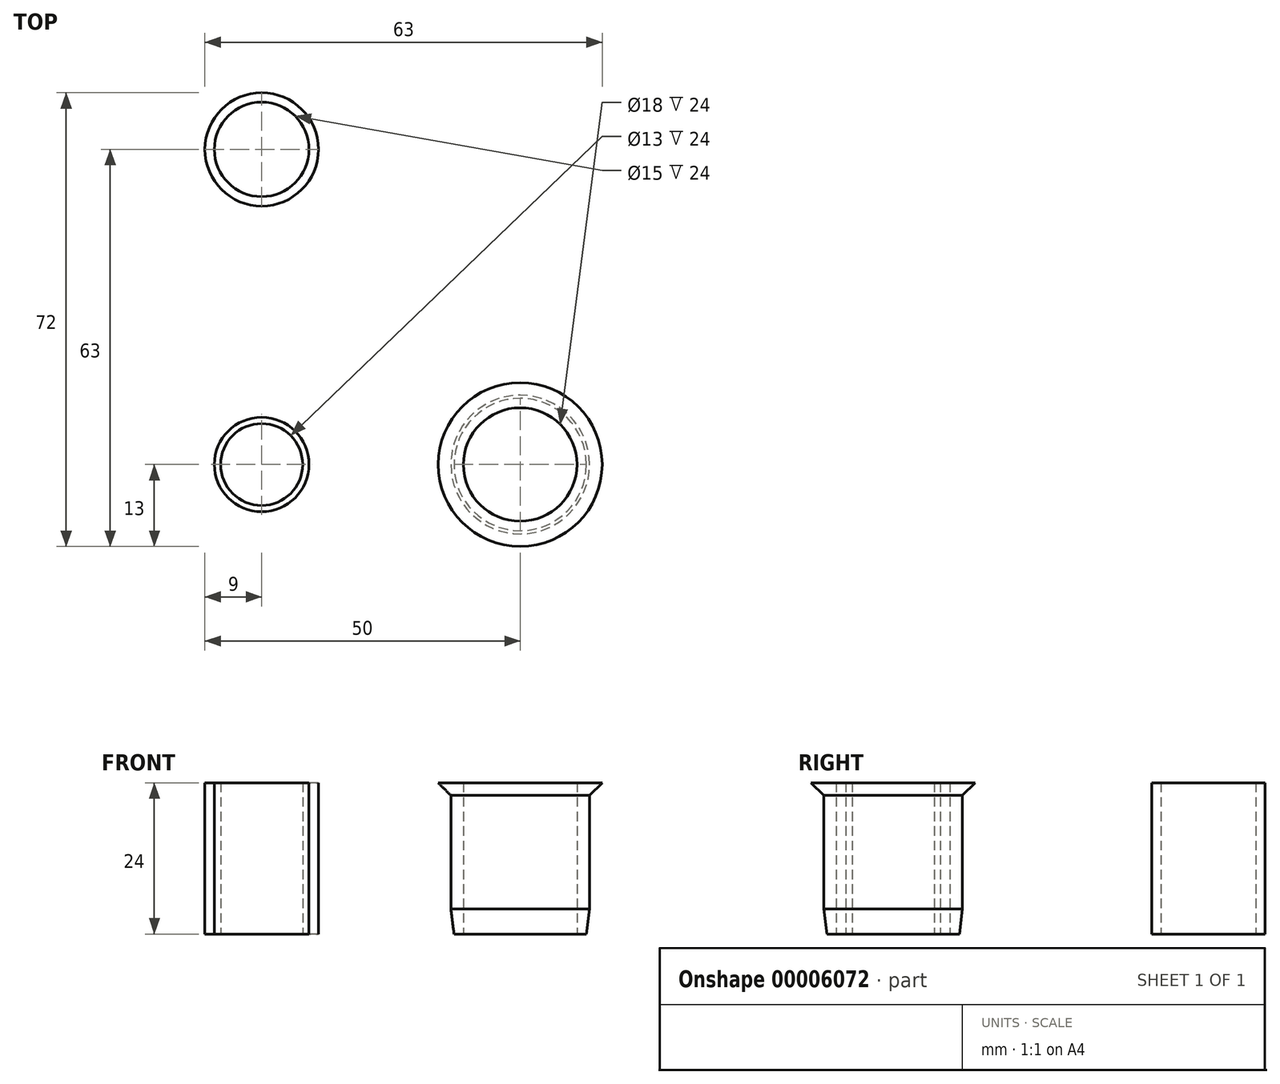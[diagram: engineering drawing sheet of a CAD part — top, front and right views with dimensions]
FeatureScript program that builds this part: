
annotation { "Feature Type Name" : "Feature", "Feature Type Description" : "" }
export const myFeature = defineFeature(function(context is Context, id is Id, definition is map)
    precondition{}
    {
        {
            var Q0;
            Q0=qCreatedBy(makeId("Top.planeOp"),FACE);
            var sketch = newSketch(context, id + "F0", { "sketchPlane" : qUnion([Q0])});
            skCircle(sketch, "E0", {"center": v(0, 0) * mm, "radius": 6.5 * mm});
            skCircle(sketch, "E1", {"center": v(0, 0) * mm, "radius": 7.5 * mm});
            skLineSegment(sketch, "E2.bottom", {"start": v(0, 0) * mm, "end": v(50, 0) * mm, "construction": true});
            skLineSegment(sketch, "E2.top", {"start": v(0, 50) * mm, "end": v(50, 50) * mm, "construction": true});
            skLineSegment(sketch, "E2.left", {"start": v(0, 0) * mm, "end": v(0, 50) * mm, "construction": true});
            skLineSegment(sketch, "E2.right", {"start": v(50, 0) * mm, "end": v(50, 50) * mm, "construction": true});
            skCircle(sketch, "E3", {"center": v(0, 50) * mm, "radius": 7.5 * mm});
            skCircle(sketch, "E4", {"center": v(0, 50) * mm, "radius": 9 * mm});
            skLineSegment(sketch, "E5.bottom", {"start": v(50, 0) * mm, "end": v(54, 0) * mm});
            skLineSegment(sketch, "E5.top", {"start": v(50, 24) * mm, "end": v(54, 24) * mm});
            skLineSegment(sketch, "E5.left", {"start": v(50, 0) * mm, "end": v(50, 24) * mm});
            skLineSegment(sketch, "E5.right", {"start": v(54, 0) * mm, "end": v(54, 24) * mm});
            skLineSegment(sketch, "E6", {"start": v(54, 24) * mm, "end": v(56, 24) * mm});
            skLineSegment(sketch, "E7", {"start": v(56, 24) * mm, "end": v(54, 22) * mm});
            skLineSegment(sketch, "E8", {"start": v(54, 22) * mm, "end": v(54, 24) * mm});
            skSolve(sketch);
        }
        {
            var Q0;
            Q0=makeQuery(id+"F0.imprint","IMPRINT",FACE,{"disambiguationData":[TD([[makeQuery(id+"F0.imprint","IMPRINT",EDGE,{"derivedFrom":sQuery(id+"F0.wireOp",EDGE,"E0")}),-1.0]])]});
            var Q1;
            Q1=makeQuery(id+"F0.imprint","IMPRINT",FACE,{"disambiguationData":[TD([[makeQuery(id+"F0.imprint","IMPRINT",EDGE,{"derivedFrom":sQuery(id+"F0.wireOp",EDGE,"E3")}),-1.0]])]});
            extrude(context, id + "F1", {"entities" : qUnion([Q0, Q1]), "depth" : 24 * mm});
        }
        {
            var Q0;
            Q0=qCreatedBy(makeId("Front.planeOp"),FACE);
            var sketch = newSketch(context, id + "F2", { "sketchPlane" : qUnion([Q0])});
            skLineSegment(sketch, "E9.bottom", {"start": v(0, 0) * mm, "end": v(50, 0) * mm, "construction": true});
            skLineSegment(sketch, "E9.top", {"start": v(0, 50) * mm, "end": v(50, 50) * mm, "construction": true});
            skLineSegment(sketch, "E9.left", {"start": v(0, 0) * mm, "end": v(0, 50) * mm, "construction": true});
            skLineSegment(sketch, "E9.right", {"start": v(50, 0) * mm, "end": v(50, 50) * mm, "construction": true});
            skLineSegment(sketch, "E10", {"start": v(50, 0) * mm, "end": v(50, 24) * mm});
            skLineSegment(sketch, "E11", {"start": v(50, 24) * mm, "end": v(54, 24) * mm});
            skLineSegment(sketch, "E12", {"start": v(54, 24) * mm, "end": v(52, 22) * mm});
            skLineSegment(sketch, "E13", {"start": v(51.5, 0) * mm, "end": v(50, 0) * mm});
            skLineSegment(sketch, "E14", {"start": v(52, 22) * mm, "end": v(52, 24) * mm, "construction": true});
            skLineSegment(sketch, "E15", {"start": v(50, 11.9) * mm, "end": v(41, 11.9) * mm, "construction": true});
            skLineSegment(sketch, "E16", {"start": v(41, 11.9) * mm, "end": v(41, 18.94) * mm, "construction": true});
            skLineSegment(sketch, "E17", {"start": v(52, 22) * mm, "end": v(52, 4) * mm});
            skLineSegment(sketch, "E18", {"start": v(52, 4) * mm, "end": v(51.5, 0) * mm});
            skSolve(sketch);
        }
        {
            var Q0;
            Q0 = qSketchRegion(id + "F2", true);
            var Q1;
            Q1=sQuery(id+"F2.wireOp",EDGE,"E16");
            revolve(context, id + "F3", {"entities" : qUnion([Q0]), "axis" : qUnion([Q1]), "revolveType" : RevolveType.FULL});
        }
    });
